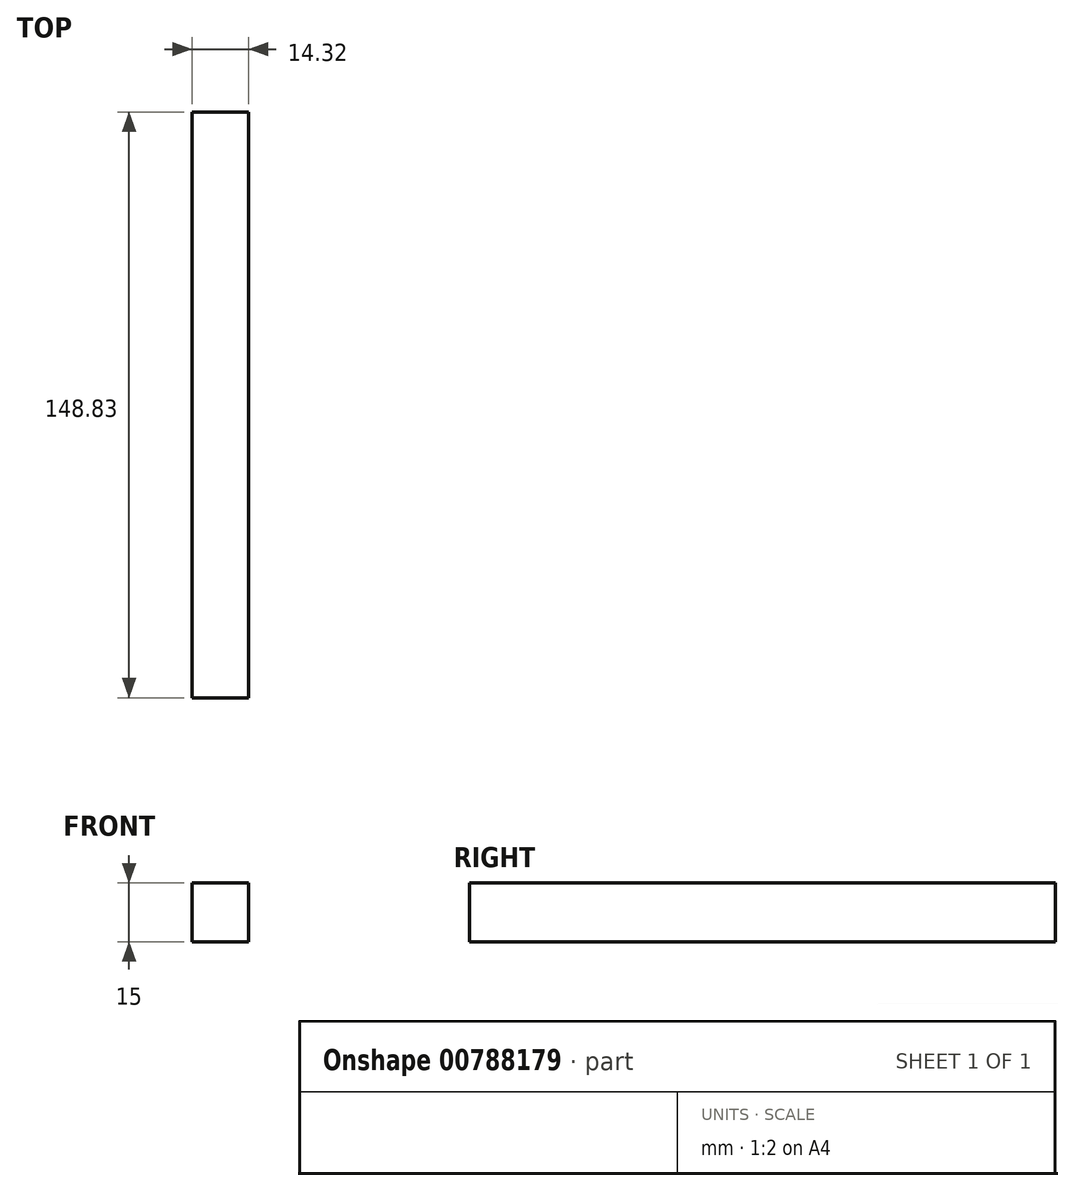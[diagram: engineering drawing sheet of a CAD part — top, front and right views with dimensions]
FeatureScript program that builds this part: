
annotation { "Feature Type Name" : "Feature", "Feature Type Description" : "" }
export const myFeature = defineFeature(function(context is Context, id is Id, definition is map)
    precondition{}
    {
        {
            var Q0;
            Q0=qCreatedBy(makeId("Top.planeOp"),FACE);
            var sketch = newSketch(context, id + "F0", { "sketchPlane" : qUnion([Q0])});
            skLineSegment(sketch, "E0.bottom", {"start": v(-72.2, -190.07) * mm, "end": v(-57.88, -190.07) * mm});
            skLineSegment(sketch, "E0.top", {"start": v(-72.2, -338.9) * mm, "end": v(-57.88, -338.9) * mm});
            skLineSegment(sketch, "E0.left", {"start": v(-72.2, -190.07) * mm, "end": v(-72.2, -338.9) * mm});
            skLineSegment(sketch, "E0.right", {"start": v(-57.88, -190.07) * mm, "end": v(-57.88, -338.9) * mm});
            skSolve(sketch);
        }
        {
            var Q0;
            Q0 = qSketchRegion(id + "F0", true);
            extrude(context, id + "F1", {"entities" : qUnion([Q0]), "depth" : 15 * mm, "offsetDistance" : 25 * mm});
        }
    });
